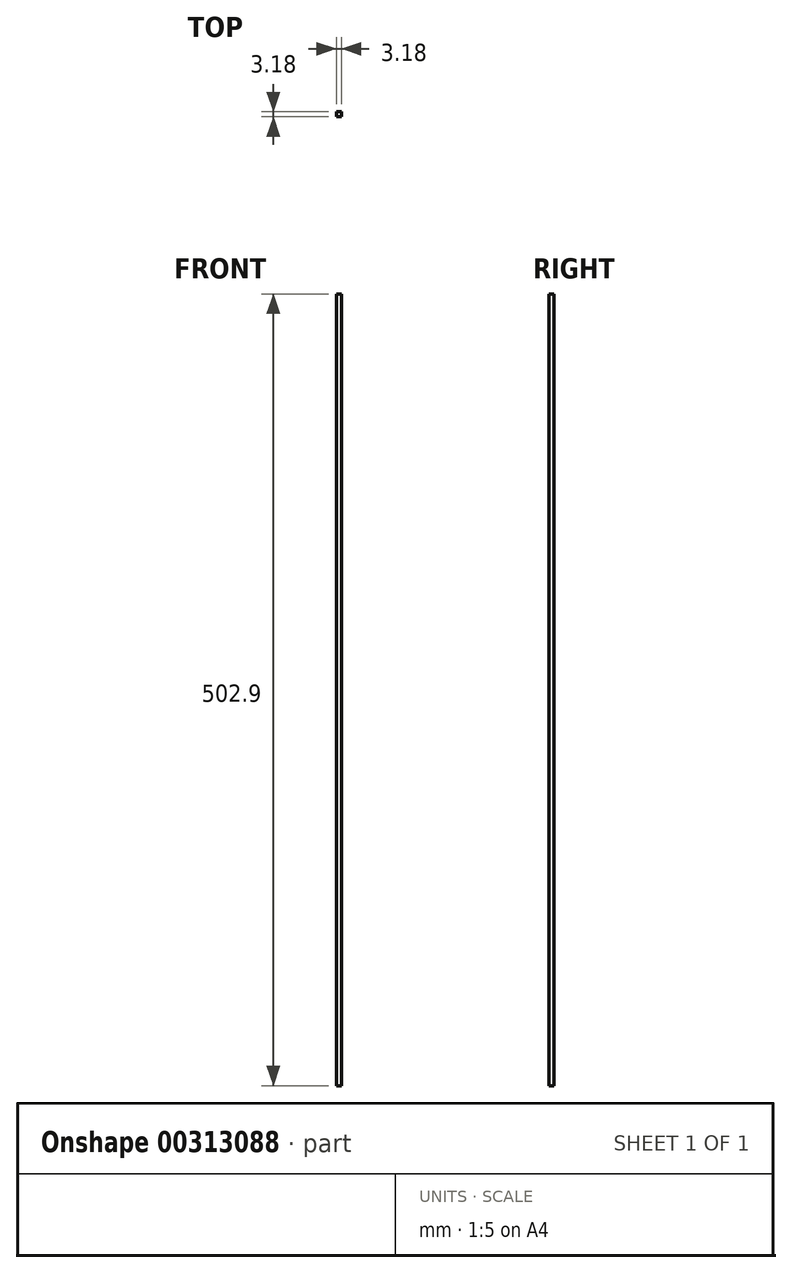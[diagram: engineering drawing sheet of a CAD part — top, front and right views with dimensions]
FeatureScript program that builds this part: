
annotation { "Feature Type Name" : "Feature", "Feature Type Description" : "" }
export const myFeature = defineFeature(function(context is Context, id is Id, definition is map)
    precondition{}
    {
        {
            var Q0;
            Q0=qCreatedBy(makeId("Top.planeOp"),FACE);
            var sketch = newSketch(context, id + "F0", { "sketchPlane" : qUnion([Q0])});
            skLineSegment(sketch, "E0.bottom", {"start": v(1.59, 1.59) * mm, "end": v(-1.59, 1.59) * mm});
            skLineSegment(sketch, "E0.top", {"start": v(1.59, -1.59) * mm, "end": v(-1.59, -1.59) * mm});
            skLineSegment(sketch, "E0.left", {"start": v(1.59, 1.59) * mm, "end": v(1.59, -1.59) * mm});
            skLineSegment(sketch, "E0.right", {"start": v(-1.59, 1.59) * mm, "end": v(-1.59, -1.59) * mm});
            skPoint(sketch, "E0.middle", {"position": v(0, 0) * mm});
            skSolve(sketch);
        }
        {
            var Q0;
            Q0 = qSketchRegion(id + "F0", true);
            extrude(context, id + "F1", {"entities" : qUnion([Q0]), "endBound" : BoundingType.SYMMETRIC, "depth" : 502.9 * mm});
        }
    });
